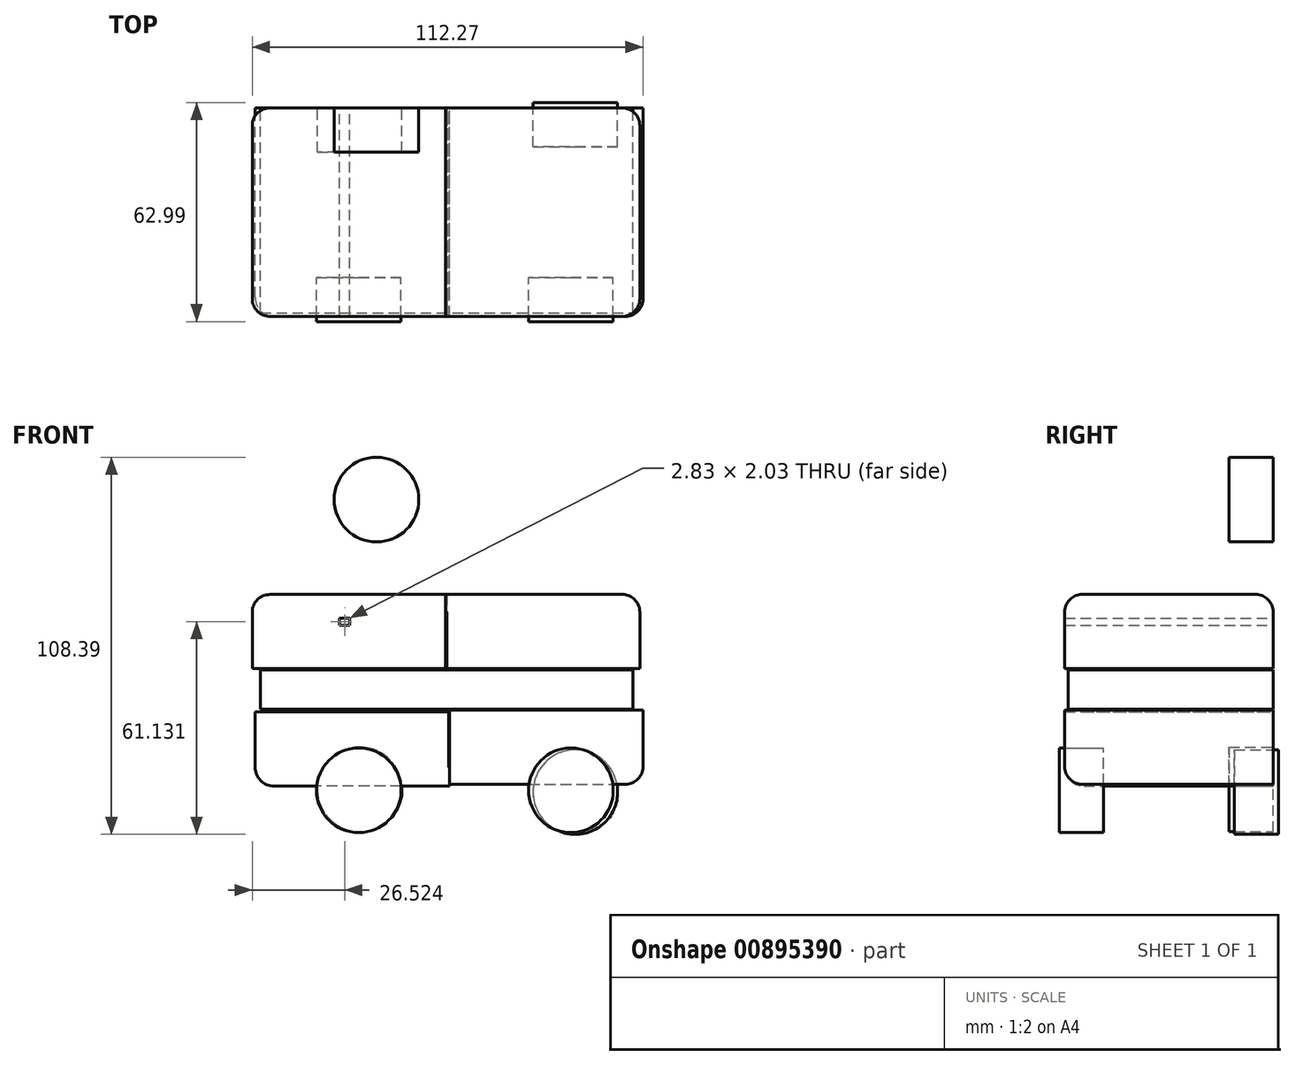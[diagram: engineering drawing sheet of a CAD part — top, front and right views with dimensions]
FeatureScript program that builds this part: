
annotation { "Feature Type Name" : "Feature", "Feature Type Description" : "" }
export const myFeature = defineFeature(function(context is Context, id is Id, definition is map)
    precondition{}
    {
        {
            var Q0;
            Q0=qCreatedBy(makeId("Front.planeOp"),FACE);
            var sketch = newSketch(context, id + "F0", { "sketchPlane" : qUnion([Q0])});
            skLineSegment(sketch, "E0.bottom", {"start": v(-53.5, 5.63) * mm, "end": v(53.5, 5.63) * mm});
            skLineSegment(sketch, "E0.top", {"start": v(-53.5, -5.63) * mm, "end": v(53.5, -5.63) * mm});
            skLineSegment(sketch, "E0.left", {"start": v(-53.5, 5.63) * mm, "end": v(-53.5, -5.63) * mm});
            skLineSegment(sketch, "E0.right", {"start": v(53.5, 5.63) * mm, "end": v(53.5, -5.63) * mm});
            skPoint(sketch, "E0.middle", {"position": v(0, 0) * mm});
            skSolve(sketch);
        }
        {
            var Q0;
            Q0 = qSketchRegion(id + "F0", true);
            extrude(context, id + "F1", {"entities" : qUnion([Q0]), "depth" : 58.93 * mm, "offsetDistance" : 25.4 * mm});
        }
        {
            var Q0;
            Q0=qCreatedBy(makeId("Front.planeOp"),FACE);
            var sketch = newSketch(context, id + "F2", { "sketchPlane" : qUnion([Q0])});
            skLineSegment(sketch, "E1.bottom", {"start": v(-55.88, 42.83) * mm, "end": v(0, 42.83) * mm});
            skLineSegment(sketch, "E1.top", {"start": v(-55.88, 21.5) * mm, "end": v(0, 21.5) * mm});
            skLineSegment(sketch, "E1.left", {"start": v(-55.88, 42.83) * mm, "end": v(-55.88, 21.5) * mm});
            skLineSegment(sketch, "E1.right", {"start": v(0, 42.83) * mm, "end": v(0, 21.5) * mm});
            skLineSegment(sketch, "E2.bottom", {"start": v(14.09, 43.12) * mm, "end": v(69.97, 43.12) * mm});
            skLineSegment(sketch, "E2.top", {"start": v(14.09, 21.78) * mm, "end": v(69.97, 21.78) * mm});
            skLineSegment(sketch, "E2.left", {"start": v(14.09, 43.12) * mm, "end": v(14.09, 21.78) * mm});
            skLineSegment(sketch, "E2.right", {"start": v(69.97, 43.12) * mm, "end": v(69.97, 21.78) * mm});
            skLineSegment(sketch, "E3.bottom", {"start": v(0, -15.55) * mm, "end": v(-55.88, -15.55) * mm});
            skLineSegment(sketch, "E3.top", {"start": v(0, -36.88) * mm, "end": v(-55.88, -36.88) * mm});
            skLineSegment(sketch, "E3.left", {"start": v(0, -15.55) * mm, "end": v(0, -36.88) * mm});
            skLineSegment(sketch, "E3.right", {"start": v(-55.88, -15.55) * mm, "end": v(-55.88, -36.88) * mm});
            skLineSegment(sketch, "E4.bottom", {"start": v(15.25, -15.55) * mm, "end": v(71.13, -15.55) * mm});
            skLineSegment(sketch, "E4.top", {"start": v(15.25, -36.88) * mm, "end": v(71.13, -36.88) * mm});
            skLineSegment(sketch, "E4.left", {"start": v(15.25, -15.55) * mm, "end": v(15.25, -36.88) * mm});
            skLineSegment(sketch, "E4.right", {"start": v(71.13, -15.55) * mm, "end": v(71.13, -36.88) * mm});
            skPoint(sketch, "E5.oppositeSnap0", {"position": v(-27.94, 21.5) * mm});
            skLineSegment(sketch, "E5.bottom", {"start": v(-30.77, 33.98) * mm, "end": v(-27.94, 33.98) * mm});
            skLineSegment(sketch, "E5.top", {"start": v(-30.77, 36.01) * mm, "end": v(-27.94, 36.01) * mm});
            skLineSegment(sketch, "E5.left", {"start": v(-30.77, 33.98) * mm, "end": v(-30.77, 36.01) * mm});
            skLineSegment(sketch, "E5.right", {"start": v(-27.94, 33.98) * mm, "end": v(-27.94, 36.01) * mm});
            skSolve(sketch);
        }
        {
            var Q0;
            Q0=makeQuery(id+"F2.imprint","IMPRINT",FACE,{"disambiguationData":[TD([[makeQuery(id+"F2.imprint","IMPRINT",EDGE,{"derivedFrom":sQuery(id+"F2.wireOp",EDGE,"E1.bottom")}),-1.0]])]});
            var Q1;
            Q1=makeQuery(id+"F2.imprint","IMPRINT",FACE,{"disambiguationData":[TD([[makeQuery(id+"F2.imprint","IMPRINT",EDGE,{"derivedFrom":sQuery(id+"F2.wireOp",EDGE,"E2.bottom")}),-1.0]])]});
            var Q2;
            Q2=makeQuery(id+"F2.imprint","IMPRINT",FACE,{"disambiguationData":[TD([[makeQuery(id+"F2.imprint","IMPRINT",EDGE,{"derivedFrom":sQuery(id+"F2.wireOp",EDGE,"E3.bottom")}),1.0]])]});
            var Q3;
            Q3=makeQuery(id+"F2.imprint","IMPRINT",FACE,{"disambiguationData":[TD([[makeQuery(id+"F2.imprint","IMPRINT",EDGE,{"derivedFrom":sQuery(id+"F2.wireOp",EDGE,"E4.bottom")}),-1.0]])]});
            extrude(context, id + "F3", {"entities" : qUnion([Q0, Q1, Q2, Q3]), "depth" : 59.94 * mm, "offsetDistance" : 25.4 * mm});
        }
        {
            var Q0;
            Q0=makeQuery(id+"F3.opExtrude","SWEPT_BODY",BODY,{"disambiguationData":[OSD([sQuery(id+"F2.wireOp",EDGE,"E1.bottom"),sQuery(id+"F2.wireOp",EDGE,"E1.top"),sQuery(id+"F2.wireOp",EDGE,"E1.left"),sQuery(id+"F2.wireOp",EDGE,"E1.right"),sQuery(id+"F2.wireOp",EDGE,"E5.bottom"),sQuery(id+"F2.wireOp",EDGE,"E5.top"),sQuery(id+"F2.wireOp",EDGE,"E5.left"),sQuery(id+"F2.wireOp",EDGE,"E5.right")])]});
            transform(context, id + "F4", {"entities" : qUnion([Q0]), "transformType" : TransformType.TRANSLATION_3D, "dx" : 0 * mm, "dy" : 0 * mm, "dz" : -15.5 * mm, "makeCopy" : true});
        }
        {
            var Q0;
            Q0=makeQuery(id+"F3.opExtrude","SWEPT_BODY",BODY,{"disambiguationData":[OSD([sQuery(id+"F2.wireOp",EDGE,"E1.bottom"),sQuery(id+"F2.wireOp",EDGE,"E1.top"),sQuery(id+"F2.wireOp",EDGE,"E1.left"),sQuery(id+"F2.wireOp",EDGE,"E1.right"),sQuery(id+"F2.wireOp",EDGE,"E5.bottom"),sQuery(id+"F2.wireOp",EDGE,"E5.top"),sQuery(id+"F2.wireOp",EDGE,"E5.left"),sQuery(id+"F2.wireOp",EDGE,"E5.right")])]});
            deleteBodies(context, id + "F5", {"entities" : qUnion([Q0])});
        }
        {
            var Q0;
            Q0=makeQuery(id+"F4.opPattern","COPY",EDGE,{"derivedFrom":makeQuery(id+"F3.opExtrude","CAP_EDGE",EDGE,{"disambiguationData":[OSD([sQuery(id+"F2.wireOp",EDGE,"E1.left")])],"isStart":false}),"instanceName":"1"});
            var Q1;
            Q1=makeQuery(id+"F4.opPattern","COPY",EDGE,{"derivedFrom":makeQuery(id+"F3.opExtrude","CAP_EDGE",EDGE,{"disambiguationData":[OSD([sQuery(id+"F2.wireOp",EDGE,"E1.bottom")])],"isStart":false}),"instanceName":"1"});
            fillet(context, id + "F6", {"entities" : qUnion([Q0, Q1]), "radius" : 5.08 * mm, "tangentPropagation" : true, "allowEdgeOverflow" : false});
        }
        {
            var Q0;
            Q0=makeQuery(id+"F4.opPattern","COPY",EDGE,{"derivedFrom":makeQuery(id+"F3.opExtrude","SWEPT_EDGE",EDGE,{"disambiguationData":[OSD([sQuery(id+"F2.wireOp",EDGE,"E1.bottom"),sQuery(id+"F2.wireOp",EDGE,"E1.left")])]}),"instanceName":"1"});
            fillet(context, id + "F7", {"entities" : qUnion([Q0]), "radius" : 5.08 * mm, "tangentPropagation" : true, "allowEdgeOverflow" : false});
        }
        {
            var Q0;
            Q0=makeQuery(id+"F3.opExtrude","CAP_EDGE",EDGE,{"disambiguationData":[OSD([sQuery(id+"F2.wireOp",EDGE,"E2.bottom")])],"isStart":false});
            var Q1;
            Q1=makeQuery(id+"F3.opExtrude","SWEPT_EDGE",EDGE,{"disambiguationData":[OSD([sQuery(id+"F2.wireOp",EDGE,"E2.bottom"),sQuery(id+"F2.wireOp",EDGE,"E2.right")])]});
            var Q2;
            Q2=makeQuery(id+"F3.opExtrude","CAP_EDGE",EDGE,{"disambiguationData":[OSD([sQuery(id+"F2.wireOp",EDGE,"E2.right")])],"isStart":false});
            fillet(context, id + "F8", {"entities" : qUnion([Q0, Q1, Q2]), "radius" : 5.08 * mm, "tangentPropagation" : true, "allowEdgeOverflow" : false});
        }
        {
            var Q0;
            Q0=makeQuery(id+"F3.opExtrude","SWEPT_BODY",BODY,{"disambiguationData":[OSD([sQuery(id+"F2.wireOp",EDGE,"E2.bottom"),sQuery(id+"F2.wireOp",EDGE,"E2.top"),sQuery(id+"F2.wireOp",EDGE,"E2.left"),sQuery(id+"F2.wireOp",EDGE,"E2.right")])]});
            transform(context, id + "F9", {"entities" : qUnion([Q0]), "transformType" : TransformType.TRANSLATION_3D, "dx" : -14.48 * mm, "dy" : 0 * mm, "dz" : -15.75 * mm, "makeCopy" : true});
        }
        {
            var Q0;
            Q0=makeQuery(id+"F3.opExtrude","SWEPT_BODY",BODY,{"disambiguationData":[OSD([sQuery(id+"F2.wireOp",EDGE,"E2.bottom"),sQuery(id+"F2.wireOp",EDGE,"E2.top"),sQuery(id+"F2.wireOp",EDGE,"E2.left"),sQuery(id+"F2.wireOp",EDGE,"E2.right")])]});
            deleteBodies(context, id + "F10", {"entities" : qUnion([Q0])});
        }
        {
            var Q0;
            Q0=makeQuery(id+"F3.opExtrude","SWEPT_BODY",BODY,{"disambiguationData":[OSD([sQuery(id+"F2.wireOp",EDGE,"E3.bottom"),sQuery(id+"F2.wireOp",EDGE,"E3.top"),sQuery(id+"F2.wireOp",EDGE,"E3.left"),sQuery(id+"F2.wireOp",EDGE,"E3.right")])]});
            transform(context, id + "F11", {"entities" : qUnion([Q0]), "transformType" : TransformType.TRANSLATION_3D, "dx" : 0.76 * mm, "dy" : 0 * mm, "dz" : 9.14 * mm, "makeCopy" : true});
        }
        {
            var Q0;
            Q0=makeQuery(id+"F3.opExtrude","SWEPT_BODY",BODY,{"disambiguationData":[OSD([sQuery(id+"F2.wireOp",EDGE,"E3.bottom"),sQuery(id+"F2.wireOp",EDGE,"E3.top"),sQuery(id+"F2.wireOp",EDGE,"E3.left"),sQuery(id+"F2.wireOp",EDGE,"E3.right")])]});
            deleteBodies(context, id + "F12", {"entities" : qUnion([Q0])});
        }
        {
            var Q0;
            Q0=makeQuery(id+"F3.opExtrude","SWEPT_BODY",BODY,{"disambiguationData":[OSD([sQuery(id+"F2.wireOp",EDGE,"E4.bottom"),sQuery(id+"F2.wireOp",EDGE,"E4.top"),sQuery(id+"F2.wireOp",EDGE,"E4.left"),sQuery(id+"F2.wireOp",EDGE,"E4.right")])]});
            transform(context, id + "F13", {"entities" : qUnion([Q0]), "transformType" : TransformType.TRANSLATION_3D, "dx" : -14.73 * mm, "dy" : 0 * mm, "dz" : 9.65 * mm, "makeCopy" : true});
        }
        {
            var Q0;
            Q0=makeQuery(id+"F3.opExtrude","SWEPT_BODY",BODY,{"disambiguationData":[OSD([sQuery(id+"F2.wireOp",EDGE,"E4.bottom"),sQuery(id+"F2.wireOp",EDGE,"E4.top"),sQuery(id+"F2.wireOp",EDGE,"E4.left"),sQuery(id+"F2.wireOp",EDGE,"E4.right")])]});
            deleteBodies(context, id + "F14", {"entities" : qUnion([Q0])});
        }
        {
            var Q0;
            Q0=makeQuery(id+"F13.opPattern","COPY",EDGE,{"derivedFrom":makeQuery(id+"F3.opExtrude","SWEPT_EDGE",EDGE,{"disambiguationData":[OSD([sQuery(id+"F2.wireOp",EDGE,"E4.top"),sQuery(id+"F2.wireOp",EDGE,"E4.right")])]}),"instanceName":"1"});
            var Q1;
            Q1=makeQuery(id+"F13.opPattern","COPY",EDGE,{"derivedFrom":makeQuery(id+"F3.opExtrude","CAP_EDGE",EDGE,{"disambiguationData":[OSD([sQuery(id+"F2.wireOp",EDGE,"E4.right")])],"isStart":false}),"instanceName":"1"});
            fillet(context, id + "F15", {"entities" : qUnion([Q0, Q1]), "radius" : 5.08 * mm, "tangentPropagation" : true, "allowEdgeOverflow" : false});
        }
        {
            var Q0;
            Q0=makeQuery(id+"F13.opPattern","COPY",EDGE,{"derivedFrom":makeQuery(id+"F3.opExtrude","CAP_EDGE",EDGE,{"disambiguationData":[OSD([sQuery(id+"F2.wireOp",EDGE,"E4.top")])],"isStart":false}),"instanceName":"1"});
            fillet(context, id + "F16", {"entities" : qUnion([Q0]), "radius" : 5.08 * mm, "tangentPropagation" : true, "allowEdgeOverflow" : false});
        }
        {
            var Q0;
            Q0=makeQuery(id+"F11.opPattern","COPY",EDGE,{"derivedFrom":makeQuery(id+"F3.opExtrude","CAP_EDGE",EDGE,{"disambiguationData":[OSD([sQuery(id+"F2.wireOp",EDGE,"E3.top")])],"isStart":false}),"instanceName":"1"});
            var Q1;
            Q1=makeQuery(id+"F11.opPattern","COPY",EDGE,{"derivedFrom":makeQuery(id+"F3.opExtrude","CAP_EDGE",EDGE,{"disambiguationData":[OSD([sQuery(id+"F2.wireOp",EDGE,"E3.right")])],"isStart":false}),"instanceName":"1"});
            var Q2;
            Q2=makeQuery(id+"F11.opPattern","COPY",EDGE,{"derivedFrom":makeQuery(id+"F3.opExtrude","SWEPT_EDGE",EDGE,{"disambiguationData":[OSD([sQuery(id+"F2.wireOp",EDGE,"E3.top"),sQuery(id+"F2.wireOp",EDGE,"E3.right")])]}),"instanceName":"1"});
            fillet(context, id + "F17", {"entities" : qUnion([Q0, Q1, Q2]), "radius" : 5.52 * mm, "tangentPropagation" : true, "allowEdgeOverflow" : false});
        }
        {
            var Q0;
            Q0=qCreatedBy(makeId("Front.planeOp"),FACE);
            var sketch = newSketch(context, id + "F18", { "sketchPlane" : qUnion([Q0])});
            skCircle(sketch, "E6", {"center": v(-20.18, 54.6) * mm, "radius": 12.16 * mm});
            skSolve(sketch);
        }
        {
            var Q0;
            Q0 = qSketchRegion(id + "F18", true);
            extrude(context, id + "F19", {"entities" : qUnion([Q0]), "depth" : 12.7 * mm, "offsetDistance" : 25.4 * mm});
        }
        {
            var Q0;
            Q0=makeQuery(id+"F19.opExtrude","SWEPT_BODY",BODY,{"disambiguationData":[OSD([sQuery(id+"F18.wireOp",EDGE,"E6")])]});
            transform(context, id + "F20", {"entities" : qUnion([Q0]), "transformType" : TransformType.TRANSLATION_3D, "dx" : -5.08 * mm, "dy" : -48.77 * mm, "dz" : -83.57 * mm, "makeCopy" : true});
        }
        {
            var Q0;
            Q0=makeQuery(id+"F19.opExtrude","SWEPT_BODY",BODY,{"disambiguationData":[OSD([sQuery(id+"F18.wireOp",EDGE,"E6")])]});
            transform(context, id + "F21", {"entities" : qUnion([Q0]), "transformType" : TransformType.TRANSLATION_3D, "dx" : 55.88 * mm, "dy" : -48.77 * mm, "dz" : -83.57 * mm, "makeCopy" : true});
        }
        {
            var Q0;
            Q0=makeQuery(id+"F4.opPattern","COPY",EDGE,{"derivedFrom":makeQuery(id+"F3.opExtrude","CAP_EDGE",EDGE,{"disambiguationData":[OSD([sQuery(id+"F2.wireOp",EDGE,"E1.left")])],"isStart":true}),"instanceName":"1"});
            var Q1;
            Q1=makeQuery(id+"F9.opPattern","COPY",EDGE,{"derivedFrom":makeQuery(id+"F3.opExtrude","CAP_EDGE",EDGE,{"disambiguationData":[OSD([sQuery(id+"F2.wireOp",EDGE,"E2.right")])],"isStart":true}),"instanceName":"1"});
            fillet(context, id + "F22", {"entities" : qUnion([Q0, Q1]), "radius" : 5.08 * mm, "tangentPropagation" : true, "allowEdgeOverflow" : false});
        }
        {
            var Q0;
            Q0=makeQuery(id+"F19.opExtrude","SWEPT_BODY",BODY,{"disambiguationData":[OSD([sQuery(id+"F18.wireOp",EDGE,"E6")])]});
            transform(context, id + "F23", {"entities" : qUnion([Q0]), "transformType" : TransformType.TRANSLATION_3D, "dx" : -4.83 * mm, "dy" : 0 * mm, "dz" : -83.31 * mm, "makeCopy" : true});
        }
        {
            var Q0;
            Q0=makeQuery(id+"F19.opExtrude","SWEPT_BODY",BODY,{"disambiguationData":[OSD([sQuery(id+"F18.wireOp",EDGE,"E6")])]});
            transform(context, id + "F24", {"entities" : qUnion([Q0]), "transformType" : TransformType.TRANSLATION_3D, "dx" : 57.15 * mm, "dy" : 1.52 * mm, "dz" : -84.07 * mm, "makeCopy" : true});
        }
    });
